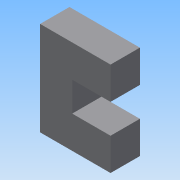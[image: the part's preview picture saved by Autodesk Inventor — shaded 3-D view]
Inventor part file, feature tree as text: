
AUTODESK INVENTOR PART (.ipt)
format: ipt  version: 2015 (Build 190159000, 159)  size: 75,776 bytes
history: native  units: mm
features: extrude x1, sketch x1
ambient origin geometry x8: Origin, YZ Plane, XZ Plane, XY Plane, X Axis, Y Axis, Z Axis, Center Point
bodies: Solid1 (feature_tree)
feature tree (2):
  extrude  "Extrusion1"  Depth=5.0mm
  sketch  "Sketch1"  dims[d0=5.0mm d1=0.0mm d2=5.0mm d3=12.0mm d4=8.0mm d5=16.0mm]
